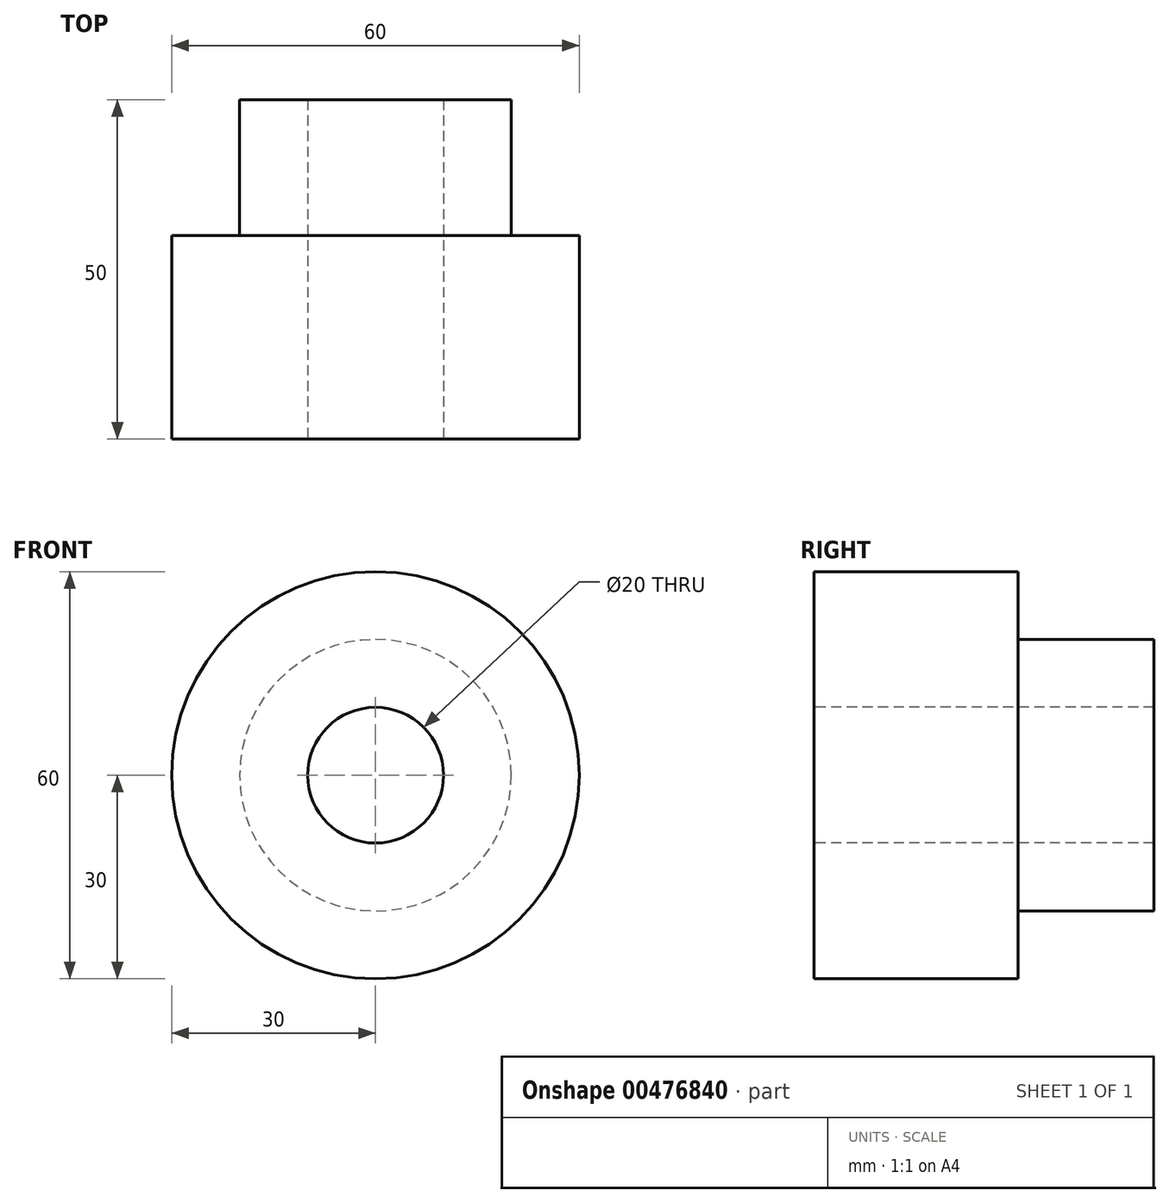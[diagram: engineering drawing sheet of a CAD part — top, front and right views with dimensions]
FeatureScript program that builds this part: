
annotation { "Feature Type Name" : "Feature", "Feature Type Description" : "" }
export const myFeature = defineFeature(function(context is Context, id is Id, definition is map)
    precondition{}
    {
        {
            var Q0;
            Q0=qCreatedBy(makeId("Front.planeOp"),FACE);
            var sketch = newSketch(context, id + "F0", { "sketchPlane" : qUnion([Q0])});
            skCircle(sketch, "E0", {"center": v(0, 0) * mm, "radius": 10 * mm});
            skCircle(sketch, "E1", {"center": v(0, 0) * mm, "radius": 30 * mm});
            skCircle(sketch, "E2", {"center": v(0, 0) * mm, "radius": 20 * mm});
            skLineSegment(sketch, "E3", {"start": v(0, 0) * mm, "end": v(0, 30) * mm});
            skSolve(sketch);
        }
        {
            var Q0;
            Q0=makeQuery(id+"F0.imprint","IMPRINT",FACE,{"disambiguationData":[TD([[makeQuery(id+"F0.imprint","IMPRINT",EDGE,{"derivedFrom":sQuery(id+"F0.wireOp",EDGE,"E0")}),-1.0]])]});
            extrude(context, id + "F1", {"entities" : qUnion([Q0]), "depth" : -50 * mm});
        }
        {
            var Q0;
            Q0 = qSketchRegion(id + "F0", true);
            extrude(context, id + "F2", {"entities" : qUnion([Q0]), "operationType" : NewBodyOperationType.ADD, "oppositeDirection" : true, "depth" : 30 * mm});
        }
    });
